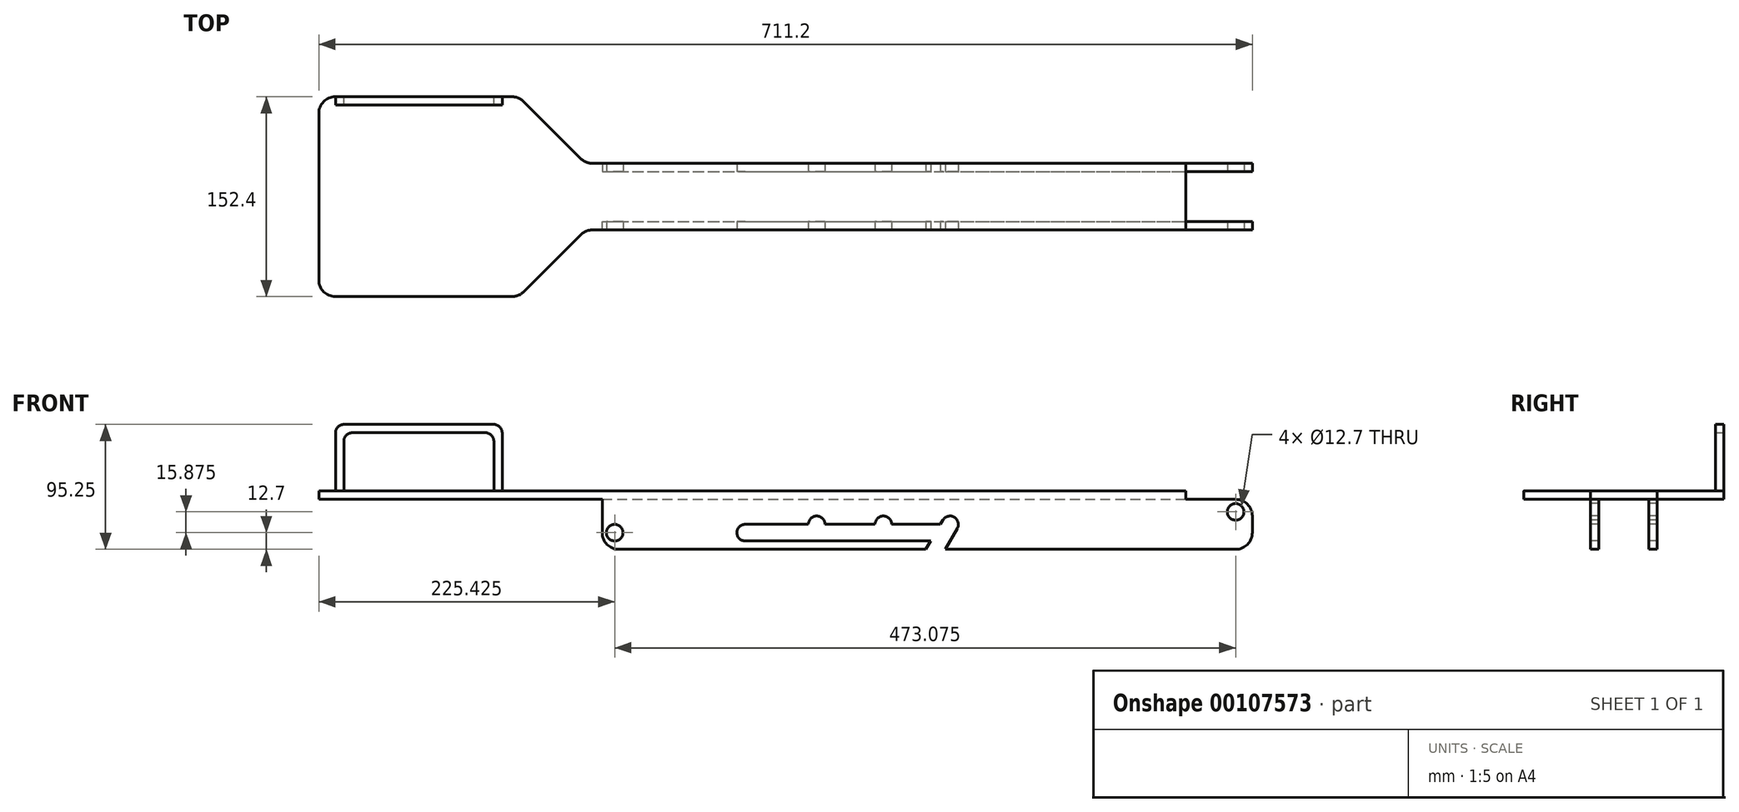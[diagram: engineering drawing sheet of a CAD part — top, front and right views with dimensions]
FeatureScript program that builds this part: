
annotation { "Feature Type Name" : "Feature", "Feature Type Description" : "" }
export const myFeature = defineFeature(function(context is Context, id is Id, definition is map)
    precondition{}
    {
        {
            var Q0;
            Q0=qCreatedBy(makeId("Top.planeOp"),FACE);
            var sketch = newSketch(context, id + "F0", { "sketchPlane" : qUnion([Q0])});
            skLineSegment(sketch, "E0.bottom", {"start": v(0, 25.4) * mm, "end": v(457.2, 25.4) * mm});
            skLineSegment(sketch, "E0.top", {"start": v(0, -25.4) * mm, "end": v(457.2, -25.4) * mm});
            skLineSegment(sketch, "E0.left", {"start": v(0, 25.4) * mm, "end": v(0, -25.4) * mm});
            skLineSegment(sketch, "E0.right", {"start": v(457.2, 25.4) * mm, "end": v(457.2, -25.4) * mm});
            skLineSegment(sketch, "E1.bottom", {"start": v(-203.2, 76.2) * mm, "end": v(-50.8, 76.2) * mm});
            skLineSegment(sketch, "E1.top", {"start": v(-203.2, -76.2) * mm, "end": v(-50.8, -76.2) * mm});
            skLineSegment(sketch, "E1.left", {"start": v(-203.2, 76.2) * mm, "end": v(-203.2, -76.2) * mm});
            skLineSegment(sketch, "E1.right", {"start": v(-50.8, 76.2) * mm, "end": v(-50.8, -76.2) * mm});
            skLineSegment(sketch, "E2", {"start": v(-50.8, 76.2) * mm, "end": v(0, 25.4) * mm});
            skLineSegment(sketch, "E3", {"start": v(-50.8, -76.2) * mm, "end": v(0, -25.4) * mm});
            skSolve(sketch);
        }
        {
            var Q0;
            Q0 = qSketchRegion(id + "F0", true);
            extrude(context, id + "F1", {"entities" : qUnion([Q0]), "oppositeDirection" : true, "depth" : 6.35 * mm});
        }
        {
            var Q0;
            Q0=makeQuery(id+"F1.opExtrude","CAP_FACE",FACE,{"disambiguationData":[OSD([sQuery(id+"F0.wireOp",EDGE,"E0.bottom"),sQuery(id+"F0.wireOp",EDGE,"E0.top"),sQuery(id+"F0.wireOp",EDGE,"E0.right"),sQuery(id+"F0.wireOp",EDGE,"E1.bottom"),sQuery(id+"F0.wireOp",EDGE,"E1.top"),sQuery(id+"F0.wireOp",EDGE,"E1.left"),sQuery(id+"F0.wireOp",EDGE,"E2"),sQuery(id+"F0.wireOp",EDGE,"E3")])],"isStart":false});
            var sketch = newSketch(context, id + "F2", { "sketchPlane" : qUnion([Q0])});
            skLineSegment(sketch, "E4.bottom", {"start": v(12.7, 25.4) * mm, "end": v(508, 25.4) * mm});
            skLineSegment(sketch, "E4.top", {"start": v(12.7, 19.05) * mm, "end": v(508, 19.05) * mm});
            skLineSegment(sketch, "E4.left", {"start": v(12.7, 25.4) * mm, "end": v(12.7, 19.05) * mm});
            skLineSegment(sketch, "E4.right", {"start": v(508, 25.4) * mm, "end": v(508, 19.05) * mm});
            skLineSegment(sketch, "E5", {"start": v(-203.2, 0) * mm, "end": v(457.2, 0) * mm, "construction": true});
            skLineSegment(sketch, "E6.MirrorCS", {"start": v(12.7, -25.4) * mm, "end": v(12.7, -19.05) * mm});
            skLineSegment(sketch, "E7.MirrorCS", {"start": v(12.7, -25.4) * mm, "end": v(508, -25.4) * mm});
            skLineSegment(sketch, "E8.MirrorCS", {"start": v(12.7, -19.05) * mm, "end": v(508, -19.05) * mm});
            skLineSegment(sketch, "E9.MirrorCS", {"start": v(508, -25.4) * mm, "end": v(508, -19.05) * mm});
            skSolve(sketch);
        }
        {
            var Q0;
            Q0 = qSketchRegion(id + "F2", true);
            extrude(context, id + "F3", {"entities" : qUnion([Q0]), "operationType" : NewBodyOperationType.ADD, "depth" : 38.1 * mm});
        }
        {
            var Q0;
            Q0=makeQuery(id+"F3.boolean.opBoolean","MERGE",FACE,{"derivedFrom":[makeQuery(id+"F1.opExtrude","SWEPT_FACE",FACE,{"disambiguationData":[OSD([sQuery(id+"F0.wireOp",EDGE,"E0.top")])]}),makeQuery(id+"F3.opExtrude","SWEPT_FACE",FACE,{"disambiguationData":[OSD([sQuery(id+"F2.wireOp",EDGE,"E4.bottom")])]})]});
            var sketch = newSketch(context, id + "F4", { "sketchPlane" : qUnion([Q0])});
            skCircle(sketch, "E10", {"center": v(495.3, -15.88) * mm, "radius": 19.05 * mm});
            skCircle(sketch, "E11", {"center": v(495.3, -15.88) * mm, "radius": 25.4 * mm});
            skCircle(sketch, "E12", {"center": v(495.3, -15.88) * mm, "radius": 6.35 * mm});
            skSolve(sketch);
        }
        {
            var Q0;
            {var subQ0=sQuery(id+"F0.wireOp",EDGE,"E0.top");Q0=makeQuery(id+"F4.imprint","IMPRINT",FACE,{"disambiguationData":[TD([[makeQuery(id+"F4.imprint","IMPRINT",EDGE,{"derivedFrom":makeQuery(id+"F1.opExtrude","CAP_EDGE",EDGE,{"disambiguationData":[OSD([subQ0])],"isStart":true})}),-1.0]])]});}
            var sketch = newSketch(context, id + "F5", { "sketchPlane" : qUnion([Q0])});
            skCircle(sketch, "E13", {"center": v(22.23, -31.75) * mm, "radius": 6.35 * mm});
            skLineSegment(sketch, "E14", {"start": v(266.7, 0) * mm, "end": v(266.7, -44.45) * mm, "construction": true});
            skLineSegment(sketch, "E15", {"start": v(266.7, -44.45) * mm, "end": v(292.36, 0) * mm, "construction": true});
            skArc(sketch, "E16", {"start": v(283.2, -28.58) * mm, "mid": v(280.87, -19.9) * mm, "end": v(272.2, -22.23) * mm});
            skLineSegment(sketch, "E17", {"start": v(272.2, -47.62) * mm, "end": v(272.2, -47.62) * mm});
            skLineSegment(sketch, "E18", {"start": v(283.2, -28.57) * mm, "end": v(274.03, -44.45) * mm});
            skLineSegment(sketch, "E19", {"start": v(272.2, -22.23) * mm, "end": v(270.37, -25.4) * mm});
            skLineSegment(sketch, "E20", {"start": v(261.2, -41.27) * mm, "end": v(259.37, -44.45) * mm});
            skLineSegment(sketch, "E21", {"start": v(259.37, -44.45) * mm, "end": v(274.03, -44.45) * mm});
            skArc(sketch, "E22", {"start": v(121.63, -25.4) * mm, "mid": v(115.28, -31.75) * mm, "end": v(121.63, -38.1) * mm});
            skLineSegment(sketch, "E23", {"start": v(121.63, -25.4) * mm, "end": v(270.37, -25.4) * mm});
            skLineSegment(sketch, "E24", {"start": v(121.63, -38.1) * mm, "end": v(263.03, -38.1) * mm});
            skLineSegment(sketch, "E25.trimOffspring", {"start": v(263.03, -38.1) * mm, "end": v(261.2, -41.27) * mm});
            skPoint(sketch, "E26.center.orphan", {"position": v(274.03, -31.75) * mm});
            skCircle(sketch, "E27", {"center": v(226.9, -25.4) * mm, "radius": 6.35 * mm});
            skCircle(sketch, "E28", {"center": v(176.1, -25.4) * mm, "radius": 6.35 * mm});
            skSolve(sketch);
        }
        {
            var Q0;
            Q0 = qSketchRegion(id + "F5", true);
            extrude(context, id + "F6", {"entities" : qUnion([Q0]), "operationType" : NewBodyOperationType.REMOVE, "endBound" : BoundingType.THROUGH_ALL, "oppositeDirection" : true, "depth" : 25.4 * mm});
        }
        {
            var Q0;
            Q0=makeQuery(id+"F3.opExtrude","CAP_EDGE",EDGE,{"disambiguationData":[OSD([sQuery(id+"F2.wireOp",EDGE,"E4.left")])],"isStart":false});
            var Q1;
            Q1=makeQuery(id+"F3.opExtrude","CAP_EDGE",EDGE,{"disambiguationData":[OSD([sQuery(id+"F2.wireOp",EDGE,"E6.MirrorCS")])],"isStart":false});
            fillet(context, id + "F7", {"entities" : qUnion([Q0, Q1]), "radius" : 12.7 * mm, "tangentPropagation" : true, "allowEdgeOverflow" : false});
        }
        {
            var Q0;
            Q0=makeQuery(id+"F3.opExtrude","CAP_EDGE",EDGE,{"disambiguationData":[OSD([sQuery(id+"F2.wireOp",EDGE,"E4.right")])],"isStart":true});
            var Q1;
            Q1=makeQuery(id+"F3.opExtrude","CAP_EDGE",EDGE,{"disambiguationData":[OSD([sQuery(id+"F2.wireOp",EDGE,"E9.MirrorCS")])],"isStart":true});
            var Q2;
            Q2=makeQuery(id+"F3.opExtrude","CAP_EDGE",EDGE,{"disambiguationData":[OSD([sQuery(id+"F2.wireOp",EDGE,"E9.MirrorCS")])],"isStart":false});
            var Q3;
            Q3=makeQuery(id+"F3.opExtrude","CAP_EDGE",EDGE,{"disambiguationData":[OSD([sQuery(id+"F2.wireOp",EDGE,"E4.right")])],"isStart":false});
            fillet(context, id + "F8", {"entities" : qUnion([Q0, Q1, Q2, Q3]), "radius" : 12.7 * mm, "tangentPropagation" : true, "allowEdgeOverflow" : false});
        }
        {
            var Q0;
            Q0=makeQuery(id+"F1.opExtrude","CAP_FACE",FACE,{"disambiguationData":[OSD([sQuery(id+"F0.wireOp",EDGE,"E0.bottom"),sQuery(id+"F0.wireOp",EDGE,"E0.top"),sQuery(id+"F0.wireOp",EDGE,"E0.right"),sQuery(id+"F0.wireOp",EDGE,"E1.bottom"),sQuery(id+"F0.wireOp",EDGE,"E1.top"),sQuery(id+"F0.wireOp",EDGE,"E1.left"),sQuery(id+"F0.wireOp",EDGE,"E2"),sQuery(id+"F0.wireOp",EDGE,"E3")])],"isStart":true});
            var sketch = newSketch(context, id + "F9", { "sketchPlane" : qUnion([Q0])});
            skLineSegment(sketch, "E29.bottom", {"start": v(-63.5, 69.85) * mm, "end": v(-190.5, 69.85) * mm});
            skLineSegment(sketch, "E29.top", {"start": v(-63.5, 76.2) * mm, "end": v(-190.5, 76.2) * mm});
            skLineSegment(sketch, "E29.left", {"start": v(-63.5, 69.85) * mm, "end": v(-63.5, 76.2) * mm});
            skLineSegment(sketch, "E29.right", {"start": v(-190.5, 69.85) * mm, "end": v(-190.5, 76.2) * mm});
            skSolve(sketch);
        }
        {
            var Q0;
            Q0 = qSketchRegion(id + "F9", true);
            extrude(context, id + "F10", {"entities" : qUnion([Q0]), "operationType" : NewBodyOperationType.ADD, "depth" : 50.8 * mm});
        }
        {
            var Q0;
            Q0=makeQuery(id+"F10.boolean.opBoolean","MERGE",FACE,{"derivedFrom":[makeQuery(id+"F1.opExtrude","SWEPT_FACE",FACE,{"disambiguationData":[OSD([sQuery(id+"F0.wireOp",EDGE,"E1.bottom")])]}),makeQuery(id+"F10.opExtrude","SWEPT_FACE",FACE,{"disambiguationData":[OSD([sQuery(id+"F9.wireOp",EDGE,"E29.top")])]})]});
            var sketch = newSketch(context, id + "F11", { "sketchPlane" : qUnion([Q0])});
            skLineSegment(sketch, "E30.bottom", {"start": v(69.85, 44.45) * mm, "end": v(184.15, 44.45) * mm});
            skLineSegment(sketch, "E30.top", {"start": v(69.85, 0) * mm, "end": v(184.15, 0) * mm});
            skLineSegment(sketch, "E30.left", {"start": v(69.85, 44.45) * mm, "end": v(69.85, 0) * mm});
            skLineSegment(sketch, "E30.right", {"start": v(184.15, 44.45) * mm, "end": v(184.15, 0) * mm});
            skSolve(sketch);
        }
        {
            var Q0;
            Q0 = qSketchRegion(id + "F11", true);
            extrude(context, id + "F12", {"entities" : qUnion([Q0]), "operationType" : NewBodyOperationType.REMOVE, "endBound" : BoundingType.UP_TO_NEXT, "oppositeDirection" : true, "depth" : 25.4 * mm});
        }
        {
            var Q0;
            Q0=makeQuery(id+"F1.opExtrude","SWEPT_EDGE",EDGE,{"disambiguationData":[OSD([sQuery(id+"F0.wireOp",EDGE,"E1.top"),sQuery(id+"F0.wireOp",EDGE,"E1.right"),sQuery(id+"F0.wireOp",EDGE,"E3")])]});
            var Q1;
            Q1=makeQuery(id+"F1.opExtrude","SWEPT_EDGE",EDGE,{"disambiguationData":[OSD([sQuery(id+"F0.wireOp",EDGE,"E1.top"),sQuery(id+"F0.wireOp",EDGE,"E1.left")])]});
            var Q2;
            Q2=makeQuery(id+"F1.opExtrude","SWEPT_EDGE",EDGE,{"disambiguationData":[OSD([sQuery(id+"F0.wireOp",EDGE,"E1.bottom"),sQuery(id+"F0.wireOp",EDGE,"E1.left")])]});
            var Q3;
            Q3=makeQuery(id+"F1.opExtrude","SWEPT_EDGE",EDGE,{"disambiguationData":[OSD([sQuery(id+"F0.wireOp",EDGE,"E1.bottom"),sQuery(id+"F0.wireOp",EDGE,"E1.right"),sQuery(id+"F0.wireOp",EDGE,"E2")])]});
            fillet(context, id + "F13", {"entities" : qUnion([Q0, Q1, Q2, Q3]), "radius" : 12.7 * mm, "tangentPropagation" : true, "allowEdgeOverflow" : false});
        }
        {
            var Q0;
            Q0=makeQuery(id+"F1.opExtrude","SWEPT_EDGE",EDGE,{"disambiguationData":[OSD([sQuery(id+"F0.wireOp",EDGE,"E0.bottom"),sQuery(id+"F0.wireOp",EDGE,"E0.left"),sQuery(id+"F0.wireOp",EDGE,"E2")])]});
            var Q1;
            Q1=makeQuery(id+"F1.opExtrude","SWEPT_EDGE",EDGE,{"disambiguationData":[OSD([sQuery(id+"F0.wireOp",EDGE,"E0.top"),sQuery(id+"F0.wireOp",EDGE,"E0.left"),sQuery(id+"F0.wireOp",EDGE,"E3")])]});
            fillet(context, id + "F14", {"entities" : qUnion([Q0, Q1]), "radius" : 12.7 * mm, "tangentPropagation" : true, "allowEdgeOverflow" : false});
        }
        {
            var Q0;
            Q0=makeQuery(id+"F10.opExtrude","CAP_EDGE",EDGE,{"disambiguationData":[OSD([sQuery(id+"F9.wireOp",EDGE,"E29.left")])],"isStart":false});
            var Q1;
            Q1=makeQuery(id+"F10.opExtrude","CAP_EDGE",EDGE,{"disambiguationData":[OSD([sQuery(id+"F9.wireOp",EDGE,"E29.right")])],"isStart":false});
            var Q2;
            Q2=makeQuery(id+"F12.boolean.opBoolean","COPY",EDGE,{"derivedFrom":makeQuery(id+"F12.opExtrude","SWEPT_EDGE",EDGE,{"disambiguationData":[OSD([sQuery(id+"F11.wireOp",EDGE,"E30.bottom"),sQuery(id+"F11.wireOp",EDGE,"E30.left")])]})});
            var Q3;
            Q3=makeQuery(id+"F12.boolean.opBoolean","COPY",EDGE,{"derivedFrom":makeQuery(id+"F12.opExtrude","SWEPT_EDGE",EDGE,{"disambiguationData":[OSD([sQuery(id+"F11.wireOp",EDGE,"E30.bottom"),sQuery(id+"F11.wireOp",EDGE,"E30.right")])]})});
            fillet(context, id + "F15", {"entities" : qUnion([Q0, Q1, Q2, Q3]), "radius" : 6.35 * mm, "tangentPropagation" : true, "allowEdgeOverflow" : false});
        }
        {
            var Q0;
            Q0=makeQuery(id+"F4.imprint","IMPRINT",FACE,{"disambiguationData":[TD([[makeQuery(id+"F4.imprint","IMPRINT",EDGE,{"derivedFrom":sQuery(id+"F4.wireOp",EDGE,"E12")}),1.0]])]});
            extrude(context, id + "F16", {"entities" : qUnion([Q0]), "operationType" : NewBodyOperationType.REMOVE, "endBound" : BoundingType.THROUGH_ALL, "oppositeDirection" : true, "depth" : 25.4 * mm});
        }
    });
